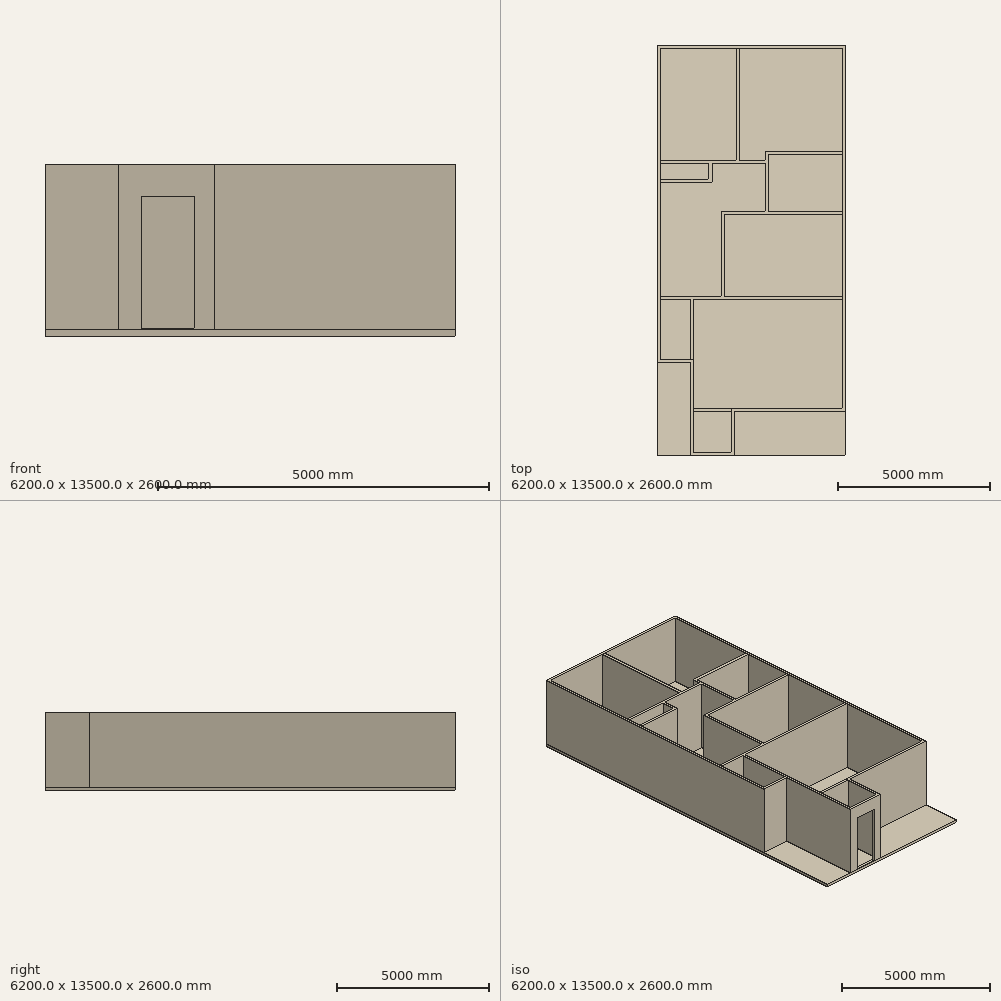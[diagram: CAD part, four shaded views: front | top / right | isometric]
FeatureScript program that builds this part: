
annotation { "Feature Type Name" : "Feature", "Feature Type Description" : "" }
export const myFeature = defineFeature(function(context is Context, id is Id, definition is map)
    precondition{}
    {
        {
            var Q0;
            Q0=qCreatedBy(makeId("Top.planeOp"),FACE);
            var sketch = newSketch(context, id + "F0", { "sketchPlane" : qUnion([Q0])});
            skLineSegment(sketch, "E0.bottom", {"start": v(-3100, -6750) * mm, "end": v(3100, -6750) * mm});
            skLineSegment(sketch, "E0.top", {"start": v(-3100, 6750) * mm, "end": v(3100, 6750) * mm});
            skLineSegment(sketch, "E0.left", {"start": v(-3100, -6750) * mm, "end": v(-3100, 6750) * mm});
            skLineSegment(sketch, "E0.right", {"start": v(3100, -6750) * mm, "end": v(3100, 6750) * mm});
            skPoint(sketch, "E0.middle", {"position": v(0, 0) * mm});
            skSolve(sketch);
        }
        {
            var Q0;
            Q0 = qSketchRegion(id + "F0", true);
            extrude(context, id + "F1", {"entities" : qUnion([Q0]), "oppositeDirection" : true, "depth" : 100 * mm});
        }
        {
            var Q0;
            Q0=qCreatedBy(makeId("Top.planeOp"),FACE);
            var sketch = newSketch(context, id + "F2", { "sketchPlane" : qUnion([Q0])});
            skLineSegment(sketch, "E1", {"start": v(-3100, -3700) * mm, "end": v(-2000, -3700) * mm});
            skLineSegment(sketch, "E2", {"start": v(-2000, -6750) * mm, "end": v(-550, -6750) * mm});
            skLineSegment(sketch, "E3", {"start": v(-550, -6750) * mm, "end": v(-550, -5300) * mm});
            skLineSegment(sketch, "E4", {"start": v(-550, -5300) * mm, "end": v(3100, -5300) * mm});
            skLineSegment(sketch, "E5", {"start": v(3100, -5300) * mm, "end": v(3100, 6750) * mm});
            skLineSegment(sketch, "E6", {"start": v(3100, 6750) * mm, "end": v(-3100, 6750) * mm});
            skLineSegment(sketch, "E7.0", {"start": v(3000, 6650) * mm, "end": v(-3000, 6650) * mm});
            skLineSegment(sketch, "E7.1", {"start": v(3000, -5200) * mm, "end": v(3000, 6650) * mm});
            skLineSegment(sketch, "E7.2", {"start": v(-3000, 6650) * mm, "end": v(-3000, -3600) * mm});
            skLineSegment(sketch, "E7.3", {"start": v(-650, -5200) * mm, "end": v(3000, -5200) * mm});
            skLineSegment(sketch, "E7.6", {"start": v(-1900, -6650) * mm, "end": v(-650, -6650) * mm});
            skLineSegment(sketch, "E7.7", {"start": v(-650, -6650) * mm, "end": v(-650, -5200) * mm});
            skLineSegment(sketch, "E8", {"start": v(-3000, -3600) * mm, "end": v(-1900, -3600) * mm});
            skLineSegment(sketch, "E9", {"start": v(-3100, -3700) * mm, "end": v(-3100, 6750) * mm});
            skLineSegment(sketch, "E10", {"start": v(-2000, -3700) * mm, "end": v(-2000, -6750) * mm});
            skLineSegment(sketch, "E11", {"start": v(-1900, -3600) * mm, "end": v(-1900, -6650) * mm});
            skSolve(sketch);
        }
        {
            var Q0;
            Q0 = qSketchRegion(id + "F2", true);
            extrude(context, id + "F3", {"entities" : qUnion([Q0]), "depth" : 2500 * mm});
        }
        {
            var Q0;
            Q0=qCreatedBy(makeId("Top.planeOp"),FACE);
            var sketch = newSketch(context, id + "F4", { "sketchPlane" : qUnion([Q0])});
            skLineSegment(sketch, "E12.bottom", {"start": v(-1900, -5300) * mm, "end": v(-650, -5300) * mm});
            skLineSegment(sketch, "E12.top", {"start": v(-1900, -5200) * mm, "end": v(-650, -5200) * mm});
            skLineSegment(sketch, "E12.left", {"start": v(-1900, -5300) * mm, "end": v(-1900, -5200) * mm});
            skLineSegment(sketch, "E12.right", {"start": v(-650, -5300) * mm, "end": v(-650, -5200) * mm});
            skSolve(sketch);
        }
        {
            var Q0;
            Q0 = qSketchRegion(id + "F4", true);
            extrude(context, id + "F5", {"entities" : qUnion([Q0]), "depth" : 2500 * mm});
        }
        {
            var Q0;
            Q0=makeQuery(id+"F3.opExtrude","SWEPT_FACE",FACE,{"disambiguationData":[OSD([sQuery(id+"F2.wireOp",EDGE,"E2")])]});
            var sketch = newSketch(context, id + "F6", { "sketchPlane" : qUnion([Q0])});
            skLineSegment(sketch, "E13.bottom", {"start": v(-1650, 20) * mm, "end": v(-850, 20) * mm});
            skLineSegment(sketch, "E13.top", {"start": v(-1650, 2020) * mm, "end": v(-850, 2020) * mm});
            skLineSegment(sketch, "E13.left", {"start": v(-1650, 20) * mm, "end": v(-1650, 2020) * mm});
            skLineSegment(sketch, "E13.right", {"start": v(-850, 20) * mm, "end": v(-850, 2020) * mm});
            skSolve(sketch);
        }
        {
            var Q0;
            Q0 = qSketchRegion(id + "F6", true);
            extrude(context, id + "F7", {"entities" : qUnion([Q0]), "operationType" : NewBodyOperationType.REMOVE, "endBound" : BoundingType.UP_TO_NEXT, "oppositeDirection" : true, "depth" : 25 * mm});
        }
        {
            var Q0;
            Q0=qCreatedBy(makeId("Top.planeOp"),FACE);
            var sketch = newSketch(context, id + "F8", { "sketchPlane" : qUnion([Q0])});
            skLineSegment(sketch, "E14", {"start": v(-2000, -3600) * mm, "end": v(-2000, -1600) * mm});
            skLineSegment(sketch, "E15", {"start": v(-2000, -1600) * mm, "end": v(-3000, -1600) * mm});
            skLineSegment(sketch, "E16", {"start": v(-3000, -1600) * mm, "end": v(-3000, -1500) * mm});
            skLineSegment(sketch, "E17", {"start": v(-3000, -1500) * mm, "end": v(-1000, -1500) * mm});
            skLineSegment(sketch, "E18", {"start": v(-1000, -1500) * mm, "end": v(-1000, 1300) * mm});
            skLineSegment(sketch, "E19", {"start": v(-1000, 1300) * mm, "end": v(450, 1300) * mm});
            skLineSegment(sketch, "E20", {"start": v(450, 1300) * mm, "end": v(450, 2850) * mm});
            skLineSegment(sketch, "E21", {"start": v(450, 2850) * mm, "end": v(-1300, 2850) * mm});
            skLineSegment(sketch, "E22", {"start": v(-1300, 2850) * mm, "end": v(-1300, 2250) * mm});
            skLineSegment(sketch, "E23", {"start": v(-1300, 2250) * mm, "end": v(-3000, 2250) * mm});
            skLineSegment(sketch, "E24", {"start": v(-3000, 2250) * mm, "end": v(-3000, 2350) * mm});
            skLineSegment(sketch, "E25", {"start": v(-3000, 2350) * mm, "end": v(-1400, 2350) * mm});
            skLineSegment(sketch, "E26", {"start": v(-1400, 2350) * mm, "end": v(-1400, 2850) * mm});
            skLineSegment(sketch, "E27", {"start": v(-1400, 2850) * mm, "end": v(-3000, 2850) * mm});
            skLineSegment(sketch, "E28", {"start": v(-3000, 2850) * mm, "end": v(-3000, 2950) * mm});
            skLineSegment(sketch, "E29", {"start": v(-3000, 2950) * mm, "end": v(-500, 2950) * mm});
            skLineSegment(sketch, "E30", {"start": v(-500, 2950) * mm, "end": v(-500, 6650) * mm});
            skLineSegment(sketch, "E31", {"start": v(-500, 6650) * mm, "end": v(-400, 6650) * mm});
            skLineSegment(sketch, "E32", {"start": v(-400, 6650) * mm, "end": v(-400, 2950) * mm});
            skLineSegment(sketch, "E33", {"start": v(-400, 2950) * mm, "end": v(450, 2950) * mm});
            skLineSegment(sketch, "E34", {"start": v(450, 2950) * mm, "end": v(450, 3250) * mm});
            skLineSegment(sketch, "E35", {"start": v(450, 3250) * mm, "end": v(3000, 3250) * mm});
            skLineSegment(sketch, "E36", {"start": v(3000, 3250) * mm, "end": v(3000, 3150) * mm});
            skLineSegment(sketch, "E37", {"start": v(3000, 3150) * mm, "end": v(550, 3150) * mm});
            skLineSegment(sketch, "E38", {"start": v(550, 3150) * mm, "end": v(550, 1300) * mm});
            skLineSegment(sketch, "E39", {"start": v(550, 1300) * mm, "end": v(3000, 1300) * mm});
            skLineSegment(sketch, "E40", {"start": v(3000, 1300) * mm, "end": v(3000, 1200) * mm});
            skLineSegment(sketch, "E41", {"start": v(3000, 1200) * mm, "end": v(-900, 1200) * mm});
            skLineSegment(sketch, "E42", {"start": v(-900, 1200) * mm, "end": v(-900, -1500) * mm});
            skLineSegment(sketch, "E43", {"start": v(-900, -1500) * mm, "end": v(3000, -1500) * mm});
            skLineSegment(sketch, "E44", {"start": v(3000, -1500) * mm, "end": v(3000, -1600) * mm});
            skLineSegment(sketch, "E45", {"start": v(3000, -1600) * mm, "end": v(-1900, -1600) * mm});
            skLineSegment(sketch, "E46", {"start": v(-1900, -1600) * mm, "end": v(-1900, -3600) * mm});
            skLineSegment(sketch, "E47", {"start": v(-1900, -3600) * mm, "end": v(-2000, -3600) * mm});
            skSolve(sketch);
        }
        {
            var Q0;
            Q0 = qSketchRegion(id + "F8", true);
            extrude(context, id + "F9", {"entities" : qUnion([Q0]), "depth" : 2500 * mm});
        }
    });
